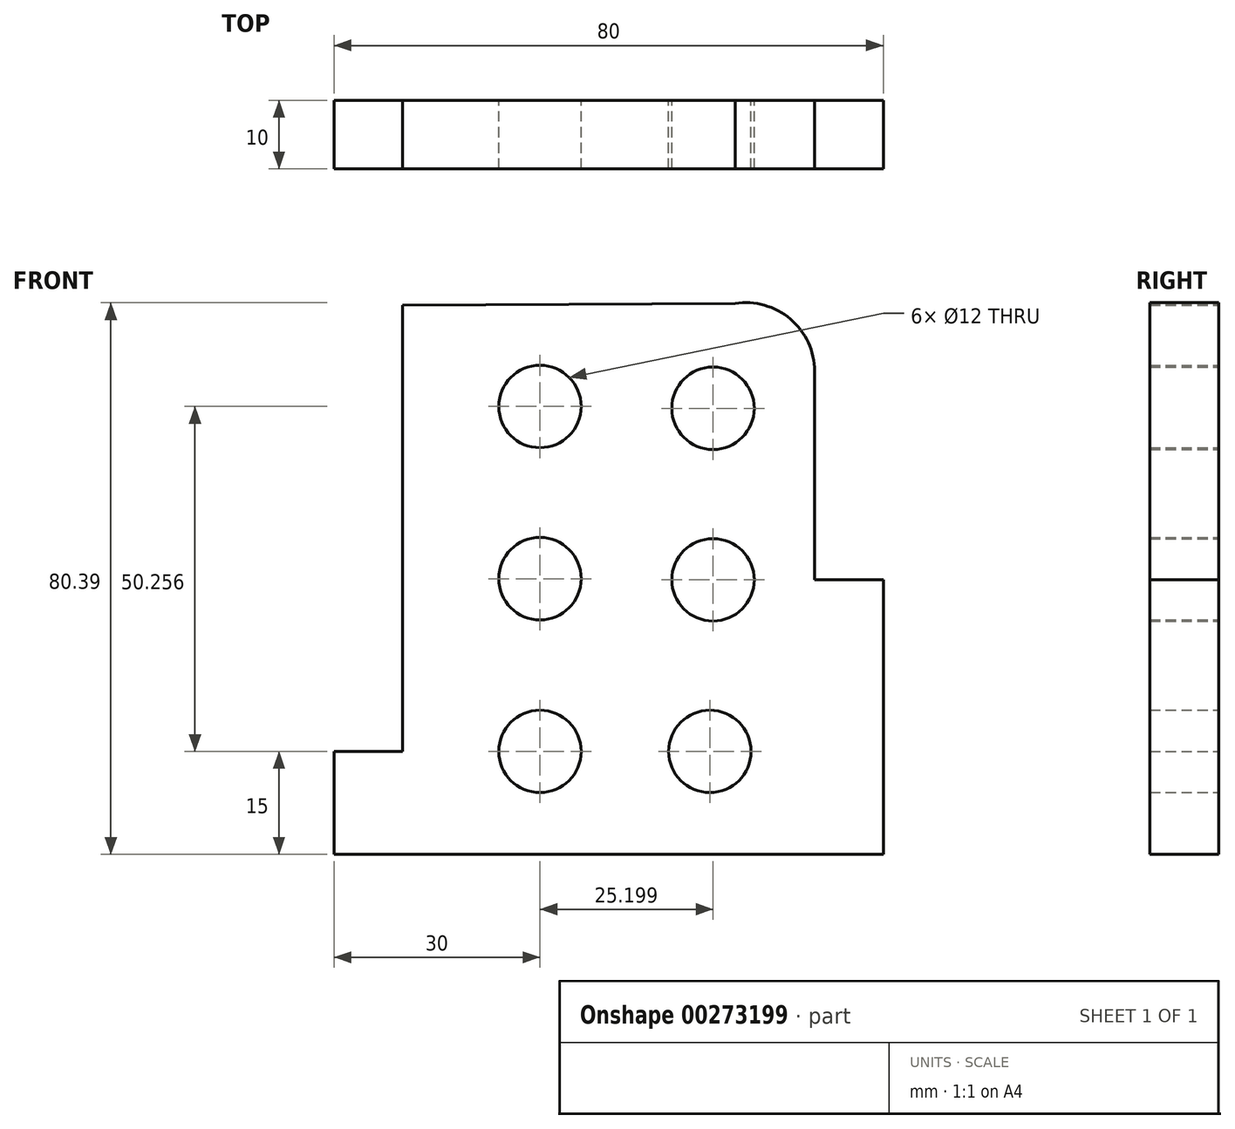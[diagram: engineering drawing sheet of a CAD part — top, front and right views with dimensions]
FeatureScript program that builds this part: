
annotation { "Feature Type Name" : "Feature", "Feature Type Description" : "" }
export const myFeature = defineFeature(function(context is Context, id is Id, definition is map)
    precondition{}
    {
        {
            var Q0;
            Q0=qCreatedBy(makeId("Front.planeOp"),FACE);
            var sketch = newSketch(context, id + "F0", { "sketchPlane" : qUnion([Q0])});
            skLineSegment(sketch, "E0", {"start": v(0, 0) * mm, "end": v(80, 0) * mm});
            skLineSegment(sketch, "E1", {"start": v(80, 0) * mm, "end": v(80, 40) * mm});
            skLineSegment(sketch, "E2", {"start": v(0, 0) * mm, "end": v(0, 15) * mm});
            skLineSegment(sketch, "E3", {"start": v(0, 15) * mm, "end": v(10, 15) * mm});
            skLineSegment(sketch, "E4", {"start": v(10, 15) * mm, "end": v(10, 80) * mm});
            skLineSegment(sketch, "E5", {"start": v(80, 40) * mm, "end": v(70, 40) * mm});
            skLineSegment(sketch, "E6", {"start": v(70, 40) * mm, "end": v(70, 70.4) * mm});
            skArc(sketch, "E7", {"start": v(70, 70.4) * mm, "mid": v(66.5, 78) * mm, "end": v(58.43, 80.27) * mm});
            skLineSegment(sketch, "E8", {"start": v(58.43, 80.27) * mm, "end": v(10, 80) * mm});
            skLineSegment(sketch, "E9", {"start": v(0, 0) * mm, "end": v(30, 0) * mm});
            skLineSegment(sketch, "E10", {"start": v(0, 0) * mm, "end": v(55, 0) * mm});
            skCircle(sketch, "E11", {"center": v(54.74, 15) * mm, "radius": 6 * mm});
            skCircle(sketch, "E12", {"center": v(30, 15) * mm, "radius": 6 * mm});
            skCircle(sketch, "E13", {"center": v(30, 40.17) * mm, "radius": 6 * mm});
            skCircle(sketch, "E14", {"center": v(55.2, 40) * mm, "radius": 6 * mm});
            skCircle(sketch, "E15", {"center": v(30, 65.26) * mm, "radius": 6 * mm});
            skCircle(sketch, "E16", {"center": v(55.2, 65) * mm, "radius": 6 * mm});
            skSolve(sketch);
        }
        {
            var Q0;
            Q0 = qSketchRegion(id + "F0", true);
            extrude(context, id + "F1", {"entities" : qUnion([Q0]), "depth" : 10 * mm});
        }
    });
